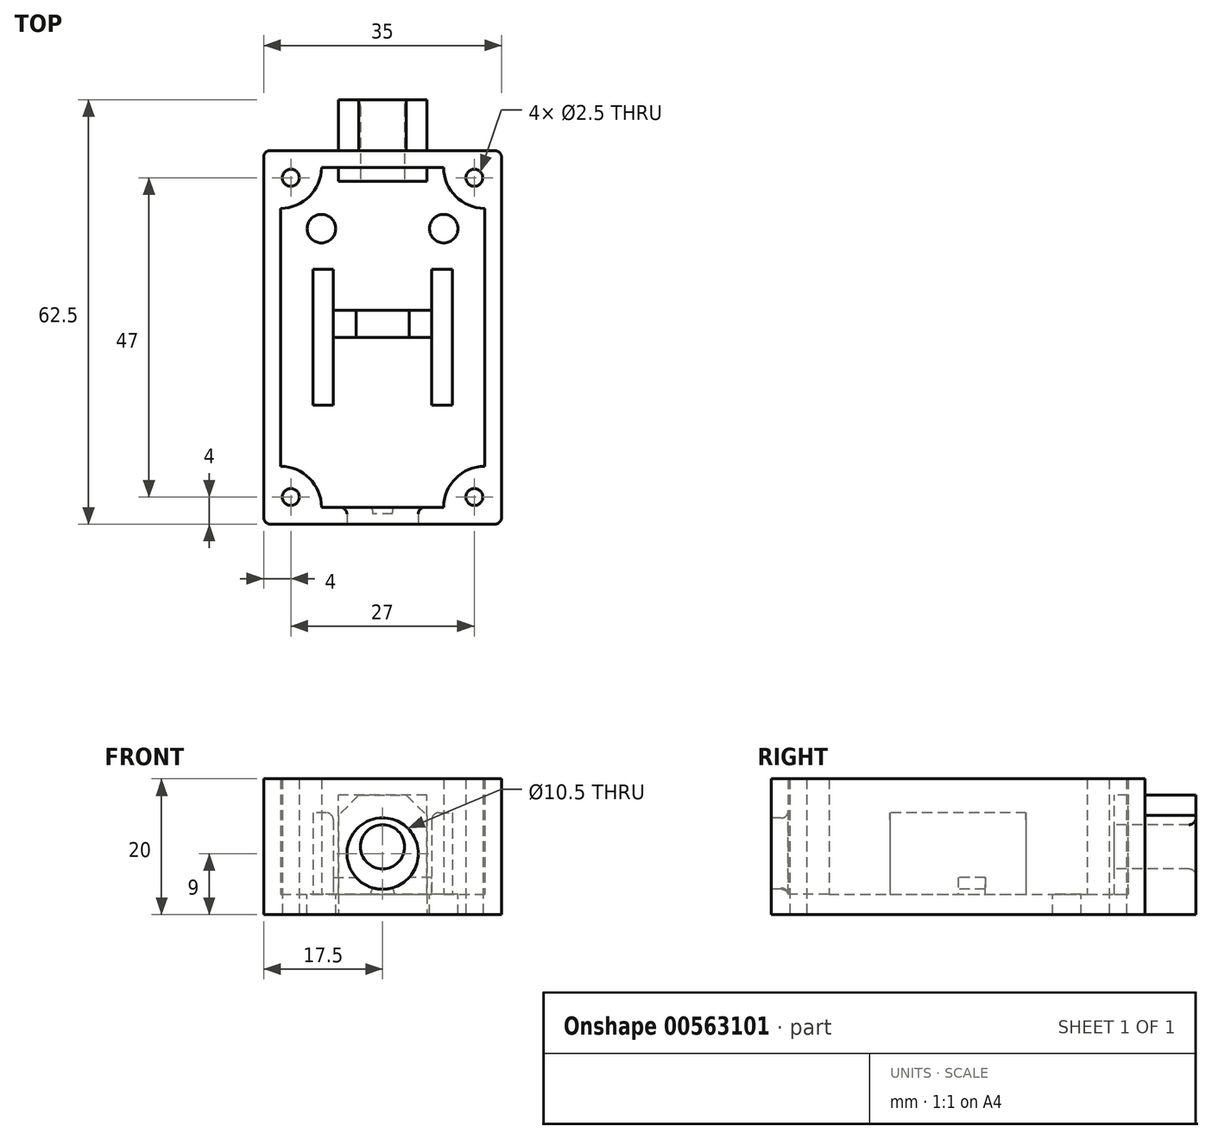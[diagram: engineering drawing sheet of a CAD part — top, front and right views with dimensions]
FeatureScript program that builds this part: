
annotation { "Feature Type Name" : "Feature", "Feature Type Description" : "" }
export const myFeature = defineFeature(function(context is Context, id is Id, definition is map)
    precondition{}
    {
        {
            var Q0;
            Q0=qCreatedBy(makeId("Top.planeOp"),FACE);
            var sketch = newSketch(context, id + "F0", { "sketchPlane" : qUnion([Q0])});
            skLineSegment(sketch, "E0.bottom", {"start": v(9, -25) * mm, "end": v(-9, -25) * mm});
            skLineSegment(sketch, "E0.top", {"start": v(9, 25) * mm, "end": v(-9, 25) * mm});
            skLineSegment(sketch, "E0.left", {"start": v(15, -19) * mm, "end": v(15, 19) * mm});
            skLineSegment(sketch, "E0.right", {"start": v(-15, -19) * mm, "end": v(-15, 19) * mm});
            skPoint(sketch, "E0.middle", {"position": v(0, 0) * mm});
            skLineSegment(sketch, "E1.bottom", {"start": v(-17.5, -27.5) * mm, "end": v(17.5, -27.5) * mm});
            skLineSegment(sketch, "E1.top", {"start": v(-17.5, 27.5) * mm, "end": v(17.5, 27.5) * mm});
            skLineSegment(sketch, "E1.left", {"start": v(-17.5, -27.5) * mm, "end": v(-17.5, 27.5) * mm});
            skLineSegment(sketch, "E1.right", {"start": v(17.5, -27.5) * mm, "end": v(17.5, 27.5) * mm});
            skArc(sketch, "E2", {"start": v(9, 25) * mm, "mid": v(10.76, 20.76) * mm, "end": v(15, 19) * mm});
            skArc(sketch, "E3", {"start": v(-9, 25) * mm, "mid": v(-10.76, 20.76) * mm, "end": v(-15, 19) * mm});
            skArc(sketch, "E4", {"start": v(-15, -19) * mm, "mid": v(-10.76, -20.76) * mm, "end": v(-9, -25) * mm});
            skArc(sketch, "E5", {"start": v(15, -19) * mm, "mid": v(10.76, -20.76) * mm, "end": v(9, -25) * mm});
            skLineSegment(sketch, "E6", {"start": v(-17.5, 27.5) * mm, "end": v(-13.5, 27.5) * mm, "construction": true});
            skLineSegment(sketch, "E7", {"start": v(-13.5, 27.5) * mm, "end": v(-13.5, 23.5) * mm, "construction": true});
            skCircle(sketch, "E8", {"center": v(-13.5, 23.5) * mm, "radius": 1.25 * mm});
            skCircle(sketch, "E9.MirrorC", {"center": v(13.5, 23.5) * mm, "radius": 1.25 * mm});
            skCircle(sketch, "E10.MirrorC", {"center": v(-13.5, -23.5) * mm, "radius": 1.25 * mm});
            skCircle(sketch, "E11.MirrorC", {"center": v(13.5, -23.5) * mm, "radius": 1.25 * mm});
            skSolve(sketch);
        }
        {
            var Q0;
            Q0=makeQuery(id+"F0.imprint","IMPRINT",FACE,{"disambiguationData":[TD([[makeQuery(id+"F0.imprint","IMPRINT",EDGE,{"derivedFrom":sQuery(id+"F0.wireOp",EDGE,"E0.bottom")}),1.0]])]});
            extrude(context, id + "F1", {"entities" : qUnion([Q0]), "depth" : 20 * mm, "offsetDistance" : 25 * mm});
        }
        {
            var Q0;
            Q0=makeQuery(id+"F0.imprint","IMPRINT",FACE,{"disambiguationData":[TD([[makeQuery(id+"F0.imprint","IMPRINT",EDGE,{"derivedFrom":sQuery(id+"F0.wireOp",EDGE,"E0.bottom")}),-1.0]])]});
            extrude(context, id + "F2", {"entities" : qUnion([Q0]), "operationType" : NewBodyOperationType.ADD, "depth" : 3 * mm, "offsetDistance" : 25 * mm});
        }
        {
            var Q0;
            Q0=makeQuery(id+"F1.opExtrude","SWEPT_EDGE",EDGE,{"disambiguationData":[OSD([sQuery(id+"F0.wireOp",EDGE,"E1.top"),sQuery(id+"F0.wireOp",EDGE,"E1.right")])]});
            var Q1;
            Q1=makeQuery(id+"F1.opExtrude","SWEPT_EDGE",EDGE,{"disambiguationData":[OSD([sQuery(id+"F0.wireOp",EDGE,"E1.top"),sQuery(id+"F0.wireOp",EDGE,"E1.left")])]});
            var Q2;
            Q2=makeQuery(id+"F1.opExtrude","SWEPT_EDGE",EDGE,{"disambiguationData":[OSD([sQuery(id+"F0.wireOp",EDGE,"E1.bottom"),sQuery(id+"F0.wireOp",EDGE,"E1.right")])]});
            var Q3;
            Q3=makeQuery(id+"F1.opExtrude","SWEPT_EDGE",EDGE,{"disambiguationData":[OSD([sQuery(id+"F0.wireOp",EDGE,"E1.bottom"),sQuery(id+"F0.wireOp",EDGE,"E1.left")])]});
            fillet(context, id + "F3", {"entities" : qUnion([Q0, Q1, Q2, Q3]), "radius" : 1 * mm, "tangentPropagation" : true, "allowEdgeOverflow" : false});
        }
        {
            var Q0;
            Q0=qCreatedBy(makeId("Top.planeOp"),FACE);
            var sketch = newSketch(context, id + "F4", { "sketchPlane" : qUnion([Q0])});
            skLineSegment(sketch, "E12.bottom", {"start": v(-7.25, -10) * mm, "end": v(7.25, -10) * mm, "construction": true});
            skLineSegment(sketch, "E12.top", {"start": v(-7.25, 10) * mm, "end": v(7.25, 10) * mm, "construction": true});
            skLineSegment(sketch, "E12.left", {"start": v(-7.25, -10) * mm, "end": v(-7.25, 10) * mm, "construction": true});
            skLineSegment(sketch, "E12.right", {"start": v(7.25, -10) * mm, "end": v(7.25, 10) * mm, "construction": true});
            skPoint(sketch, "E12.middle", {"position": v(0, 0) * mm});
            skLineSegment(sketch, "E13.bottom", {"start": v(-7.25, 10) * mm, "end": v(-10.25, 10) * mm});
            skLineSegment(sketch, "E13.top", {"start": v(-7.25, -10) * mm, "end": v(-10.25, -10) * mm});
            skLineSegment(sketch, "E13.left", {"start": v(-7.25, 10) * mm, "end": v(-7.25, -10) * mm});
            skLineSegment(sketch, "E13.right", {"start": v(-10.25, 10) * mm, "end": v(-10.25, -10) * mm});
            skLineSegment(sketch, "E14.bottom", {"start": v(7.25, 10) * mm, "end": v(10.25, 10) * mm});
            skLineSegment(sketch, "E14.top", {"start": v(7.25, -10) * mm, "end": v(10.25, -10) * mm});
            skLineSegment(sketch, "E14.left", {"start": v(7.25, 10) * mm, "end": v(7.25, -10) * mm});
            skLineSegment(sketch, "E14.right", {"start": v(10.25, 10) * mm, "end": v(10.25, -10) * mm});
            skSolve(sketch);
        }
        {
            var Q0;
            Q0 = qSketchRegion(id + "F4", true);
            extrude(context, id + "F5", {"entities" : qUnion([Q0]), "operationType" : NewBodyOperationType.ADD, "depth" : 15 * mm, "offsetDistance" : 25 * mm});
        }
        {
            var Q0;
            Q0=qCreatedBy(makeId("Top.planeOp"),FACE);
            var sketch = newSketch(context, id + "F6", { "sketchPlane" : qUnion([Q0])});
            skLineSegment(sketch, "E15", {"start": v(0, 0) * mm, "end": v(-9, 0) * mm});
            skLineSegment(sketch, "E16", {"start": v(-9, 0) * mm, "end": v(-9, 4) * mm});
            skLineSegment(sketch, "E17", {"start": v(-9, 4) * mm, "end": v(9, 4) * mm});
            skLineSegment(sketch, "E18", {"start": v(9, 4) * mm, "end": v(9, 0) * mm});
            skLineSegment(sketch, "E19", {"start": v(9, 0) * mm, "end": v(0, 0) * mm});
            skSolve(sketch);
        }
        {
            var Q0;
            Q0 = qSketchRegion(id + "F6", true);
            extrude(context, id + "F7", {"entities" : qUnion([Q0]), "operationType" : NewBodyOperationType.ADD, "depth" : 5.5 * mm, "offsetDistance" : 25 * mm});
        }
        {
            var Q0;
            Q0=qCreatedBy(makeId("Top.planeOp"),FACE);
            var sketch = newSketch(context, id + "F8", { "sketchPlane" : qUnion([Q0])});
            skLineSegment(sketch, "E20.bottom", {"start": v(9, -16) * mm, "end": v(-9, -16) * mm, "construction": true});
            skLineSegment(sketch, "E20.top", {"start": v(9, 16) * mm, "end": v(-9, 16) * mm, "construction": true});
            skLineSegment(sketch, "E20.left", {"start": v(9, -16) * mm, "end": v(9, 16) * mm, "construction": true});
            skLineSegment(sketch, "E20.right", {"start": v(-9, -16) * mm, "end": v(-9, 16) * mm, "construction": true});
            skPoint(sketch, "E20.middle", {"position": v(0, 0) * mm});
            skCircle(sketch, "E21", {"center": v(-9, 16) * mm, "radius": 2.1 * mm});
            skCircle(sketch, "E22", {"center": v(9, 16) * mm, "radius": 2.1 * mm});
            skSolve(sketch);
        }
        {
            var Q0;
            Q0 = qSketchRegion(id + "F8", true);
            extrude(context, id + "F9", {"entities" : qUnion([Q0]), "operationType" : NewBodyOperationType.REMOVE, "oppositeDirection" : true, "depth" : 25 * mm, "offsetDistance" : 25 * mm, "hasSecondDirection" : true, "secondDirectionOppositeDirection" : false, "secondDirectionDepth" : 25 * mm});
        }
        {
            var Q0;
            Q0=qCreatedBy(makeId("Front.planeOp"),FACE);
            var sketch = newSketch(context, id + "F10", { "sketchPlane" : qUnion([Q0])});
            skLineSegment(sketch, "E23", {"start": v(0, 0) * mm, "end": v(0, 9) * mm, "construction": true});
            skCircle(sketch, "E24", {"center": v(0, 9) * mm, "radius": 5.25 * mm});
            skSolve(sketch);
        }
        {
            var Q0;
            Q0 = qSketchRegion(id + "F10", true);
            extrude(context, id + "F11", {"entities" : qUnion([Q0]), "operationType" : NewBodyOperationType.REMOVE, "oppositeDirection" : true, "depth" : 25 * mm, "offsetDistance" : 25 * mm, "hasSecondDirection" : true, "secondDirectionOppositeDirection" : false, "secondDirectionDepth" : 30 * mm});
        }
        {
            var Q0;
            Q0=qCreatedBy(makeId("Front.planeOp"),FACE);
            var sketch = newSketch(context, id + "F12", { "sketchPlane" : qUnion([Q0])});
            skLineSegment(sketch, "E25", {"start": v(0, 0) * mm, "end": v(0, 10) * mm, "construction": true});
            skCircle(sketch, "E26", {"center": v(0, 10) * mm, "radius": 3.25 * mm});
            skLineSegment(sketch, "E27.bottom", {"start": v(6.5, 0) * mm, "end": v(-6.5, 0) * mm});
            skLineSegment(sketch, "E27.left", {"start": v(6.5, 0) * mm, "end": v(6.5, 17.6) * mm});
            skLineSegment(sketch, "E27.right", {"start": v(-6.5, 0) * mm, "end": v(-6.5, 17.6) * mm});
            skLineSegment(sketch, "E28", {"start": v(6.5, 17.6) * mm, "end": v(-6.5, 17.6) * mm});
            skSolve(sketch);
        }
        {
            var Q0;
            Q0 = qSketchRegion(id + "F12", true);
            extrude(context, id + "F13", {"entities" : qUnion([Q0]), "operationType" : NewBodyOperationType.ADD, "oppositeDirection" : true, "depth" : 35 * mm, "offsetDistance" : 25 * mm, "hasSecondDirection" : true, "secondDirectionOppositeDirection" : true, "secondDirectionDepth" : 23 * mm});
        }
        {
            var Q0;
            Q0=makeQuery(id+"F13.boolean.opBoolean","SPLIT",FACE,{"disambiguationData":[TD([makeQuery(id+"F13.opExtrude","SWEPT_FACE",FACE,{"disambiguationData":[OSD([sQuery(id+"F12.wireOp",EDGE,"E26")])]})])],"derivedFrom":makeQuery(id+"F1.opExtrude","SWEPT_FACE",FACE,{"disambiguationData":[OSD([sQuery(id+"F0.wireOp",EDGE,"E1.top")])]})});
            extrude(context, id + "F14", {"entities" : qUnion([Q0]), "operationType" : NewBodyOperationType.REMOVE, "oppositeDirection" : true, "depth" : 25 * mm, "offsetDistance" : 25 * mm, "hasSecondDirection" : true, "secondDirectionOppositeDirection" : false, "secondDirectionDepth" : 25 * mm});
        }
        {
            var Q0;
            {var subQ0=sQuery(id+"F12.wireOp",EDGE,"E28");var subQ1=sQuery(id+"F12.wireOp",EDGE,"E27.left");Q0=makeQuery(id+"F13.boolean.opBoolean","SPLIT",EDGE,{"disambiguationData":[TD([makeQuery(id+"F1.opExtrude","SWEPT_FACE",FACE,{"disambiguationData":[OSD([sQuery(id+"F0.wireOp",EDGE,"E1.top")])]})])],"derivedFrom":makeQuery(id+"F13.opExtrude","SWEPT_EDGE",EDGE,{"disambiguationData":[OSD([subQ1,subQ0])]})});}
            var Q1;
            {var subQ0=sQuery(id+"F12.wireOp",EDGE,"E27.right");var subQ1=sQuery(id+"F12.wireOp",EDGE,"E28");Q1=makeQuery(id+"F13.boolean.opBoolean","SPLIT",EDGE,{"disambiguationData":[TD([makeQuery(id+"F1.opExtrude","SWEPT_FACE",FACE,{"disambiguationData":[OSD([sQuery(id+"F0.wireOp",EDGE,"E1.top")])]})])],"derivedFrom":makeQuery(id+"F13.opExtrude","SWEPT_EDGE",EDGE,{"disambiguationData":[OSD([subQ0,subQ1])]})});}
            chamfer(context, id + "F15", {"entities" : qUnion([Q0, Q1]), "width" : 3 * mm, "tangentPropagation" : true});
        }
        {
            var Q0;
            Q0=makeQuery(id+"F13.opExtrude","CAP_EDGE",EDGE,{"disambiguationData":[OSD([sQuery(id+"F12.wireOp",EDGE,"E26")])],"isStart":false});
            var Q1;
            Q1=makeQuery(id+"F11.boolean.opBoolean","INTERSECT",EDGE,{"derivedFrom":[makeQuery(id+"F1.opExtrude","SWEPT_FACE",FACE,{"disambiguationData":[OSD([sQuery(id+"F0.wireOp",EDGE,"E0.bottom")])]}),makeQuery(id+"F11.opExtrude","SWEPT_FACE",FACE,{"disambiguationData":[OSD([sQuery(id+"F10.wireOp",EDGE,"E24")])]})]});
            var Q2;
            Q2=makeQuery(id+"F5.opExtrude","CAP_EDGE",EDGE,{"disambiguationData":[OSD([sQuery(id+"F4.wireOp",EDGE,"E13.left")])],"isStart":false});
            var Q3;
            Q3=makeQuery(id+"F5.opExtrude","CAP_EDGE",EDGE,{"disambiguationData":[OSD([sQuery(id+"F4.wireOp",EDGE,"E14.left")])],"isStart":false});
            fillet(context, id + "F16", {"entities" : qUnion([Q0, Q1, Q2, Q3]), "radius" : 1 * mm, "tangentPropagation" : true, "allowEdgeOverflow" : false});
        }
    });
